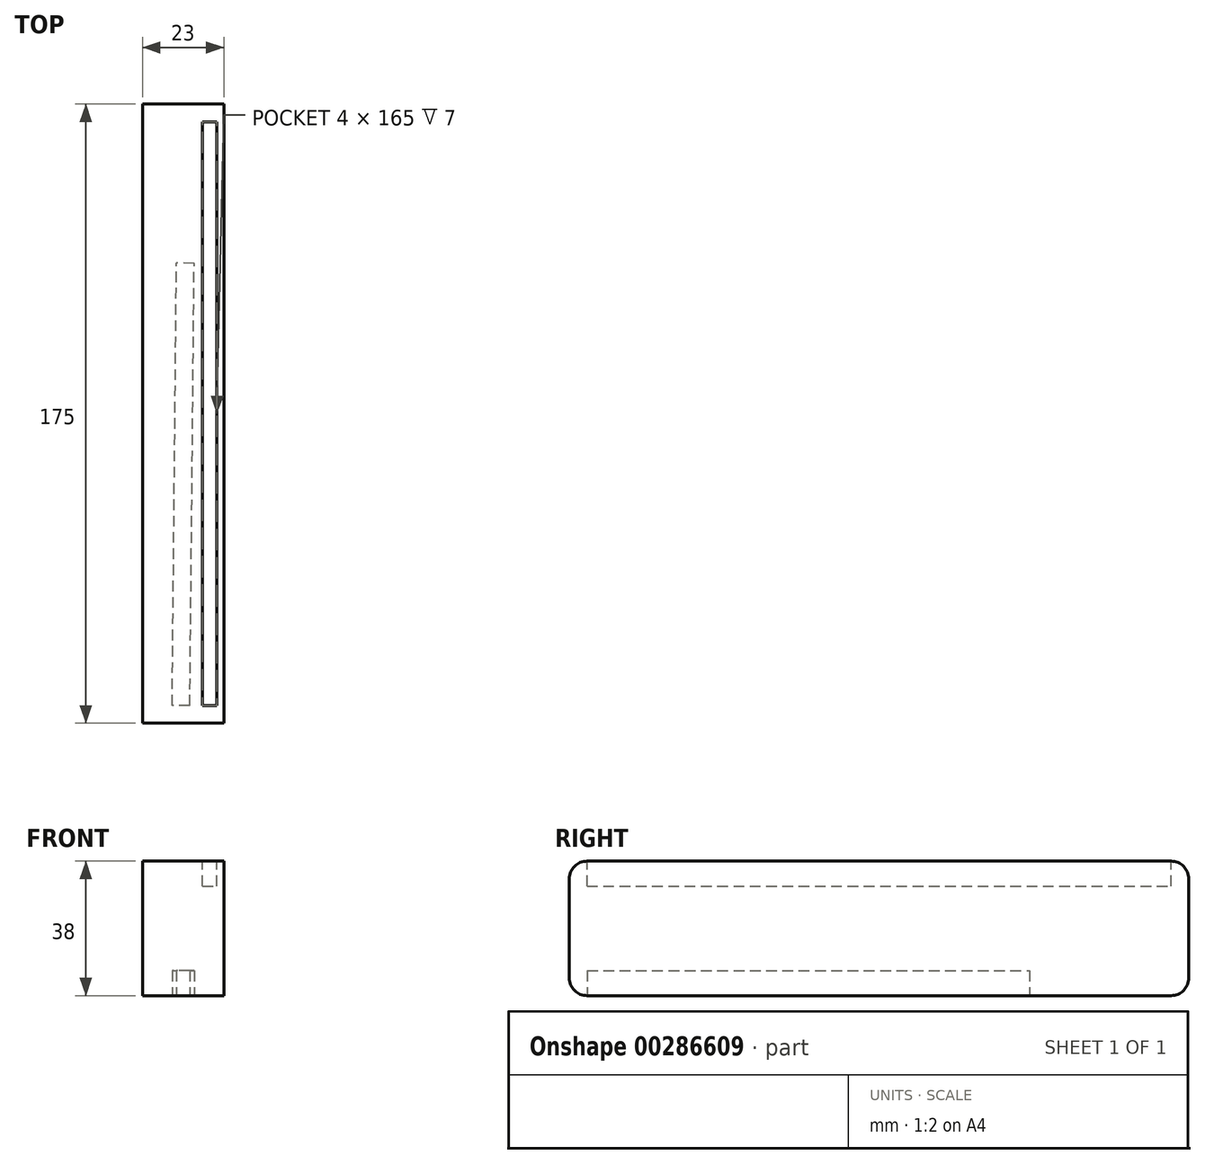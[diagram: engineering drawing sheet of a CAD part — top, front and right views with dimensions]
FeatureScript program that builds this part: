
annotation { "Feature Type Name" : "Feature", "Feature Type Description" : "" }
export const myFeature = defineFeature(function(context is Context, id is Id, definition is map)
    precondition{}
    {
        {
            var Q0;
            Q0=qCreatedBy(makeId("Front.planeOp"),FACE);
            var sketch = newSketch(context, id + "F0", { "sketchPlane" : qUnion([Q0])});
            skLineSegment(sketch, "E0.bottom", {"start": v(-11.5, 19) * mm, "end": v(11.5, 19) * mm});
            skLineSegment(sketch, "E0.top", {"start": v(-11.5, -19) * mm, "end": v(11.5, -19) * mm});
            skLineSegment(sketch, "E0.left", {"start": v(-11.5, 19) * mm, "end": v(-11.5, -19) * mm});
            skLineSegment(sketch, "E0.right", {"start": v(11.5, 19) * mm, "end": v(11.5, -19) * mm});
            skPoint(sketch, "E0.middle", {"position": v(0, 0) * mm});
            skSolve(sketch);
        }
        {
            var Q0;
            Q0=makeQuery(id+"F0.imprint","IMPRINT",FACE,{"disambiguationData":[TD([[makeQuery(id+"F0.imprint","IMPRINT",EDGE,{"derivedFrom":sQuery(id+"F0.wireOp",EDGE,"E0.bottom")}),-1.0]])]});
            extrude(context, id + "F1", {"entities" : qUnion([Q0]), "depth" : 175 * mm});
        }
        {
            var Q0;
            Q0=makeQuery(id+"F1.opExtrude","CAP_EDGE",EDGE,{"disambiguationData":[OSD([sQuery(id+"F0.wireOp",EDGE,"E0.bottom")])],"isStart":false});
            var Q1;
            Q1=makeQuery(id+"F1.opExtrude","CAP_EDGE",EDGE,{"disambiguationData":[OSD([sQuery(id+"F0.wireOp",EDGE,"E0.top")])],"isStart":false});
            var Q2;
            Q2=makeQuery(id+"F1.opExtrude","CAP_EDGE",EDGE,{"disambiguationData":[OSD([sQuery(id+"F0.wireOp",EDGE,"E0.bottom")])],"isStart":true});
            var Q3;
            Q3=makeQuery(id+"F1.opExtrude","CAP_EDGE",EDGE,{"disambiguationData":[OSD([sQuery(id+"F0.wireOp",EDGE,"E0.top")])],"isStart":true});
            fillet(context, id + "F2", {"entities" : qUnion([Q0, Q1, Q2, Q3]), "radius" : 5 * mm, "tangentPropagation" : true, "allowEdgeOverflow" : false});
        }
        {
            var Q0;
            Q0=makeQuery(id+"F1.opExtrude","SWEPT_FACE",FACE,{"disambiguationData":[OSD([sQuery(id+"F0.wireOp",EDGE,"E0.top")])]});
            var sketch = newSketch(context, id + "F3", { "sketchPlane" : qUnion([Q0])});
            skLineSegment(sketch, "E1.bottom", {"start": v(1.9, 170) * mm, "end": v(-3.1, 169.95) * mm});
            skLineSegment(sketch, "E1.top", {"start": v(3.1, 45) * mm, "end": v(-1.9, 44.96) * mm});
            skLineSegment(sketch, "E1.left", {"start": v(1.9, 170) * mm, "end": v(3.1, 45) * mm});
            skLineSegment(sketch, "E1.right", {"start": v(-3.1, 169.95) * mm, "end": v(-1.5, 4.96) * mm});
            skPoint(sketch, "E1.middle", {"position": v(0, 107.48) * mm});
            skPoint(sketch, "E1.middle.positionSnap0", {"position": v(11.5, 107.48) * mm});
            skPoint(sketch, "E1.centerSnap0", {"position": v(11.5, 107.48) * mm});
            skSolve(sketch);
        }
        {
            var Q0;
            Q0=makeQuery(id+"F3.imprint","IMPRINT",FACE,{"disambiguationData":[TD([[makeQuery(id+"F3.imprint","IMPRINT",EDGE,{"derivedFrom":sQuery(id+"F3.wireOp",EDGE,"E1.bottom")}),1.0]])]});
            extrude(context, id + "F4", {"entities" : qUnion([Q0]), "operationType" : NewBodyOperationType.REMOVE, "oppositeDirection" : true, "depth" : 7 * mm});
        }
        {
            var Q0;
            Q0=makeQuery(id+"F1.opExtrude","SWEPT_FACE",FACE,{"disambiguationData":[OSD([sQuery(id+"F0.wireOp",EDGE,"E0.bottom")])]});
            var sketch = newSketch(context, id + "F5", { "sketchPlane" : qUnion([Q0])});
            skLineSegment(sketch, "E2.bottom", {"start": v(5.5, -170) * mm, "end": v(9.5, -170) * mm});
            skLineSegment(sketch, "E2.top", {"start": v(5.5, -5) * mm, "end": v(9.5, -5) * mm});
            skLineSegment(sketch, "E2.left", {"start": v(5.5, -170) * mm, "end": v(5.5, -5) * mm});
            skLineSegment(sketch, "E2.right", {"start": v(9.5, -170) * mm, "end": v(9.5, -5) * mm});
            skSolve(sketch);
        }
        {
            var Q0;
            Q0=makeQuery(id+"F5.imprint","IMPRINT",FACE,{"disambiguationData":[TD([[makeQuery(id+"F5.imprint","IMPRINT",EDGE,{"derivedFrom":sQuery(id+"F5.wireOp",EDGE,"E2.bottom")}),1.0]])]});
            extrude(context, id + "F6", {"entities" : qUnion([Q0]), "operationType" : NewBodyOperationType.REMOVE, "oppositeDirection" : true, "depth" : 7 * mm});
        }
    });
